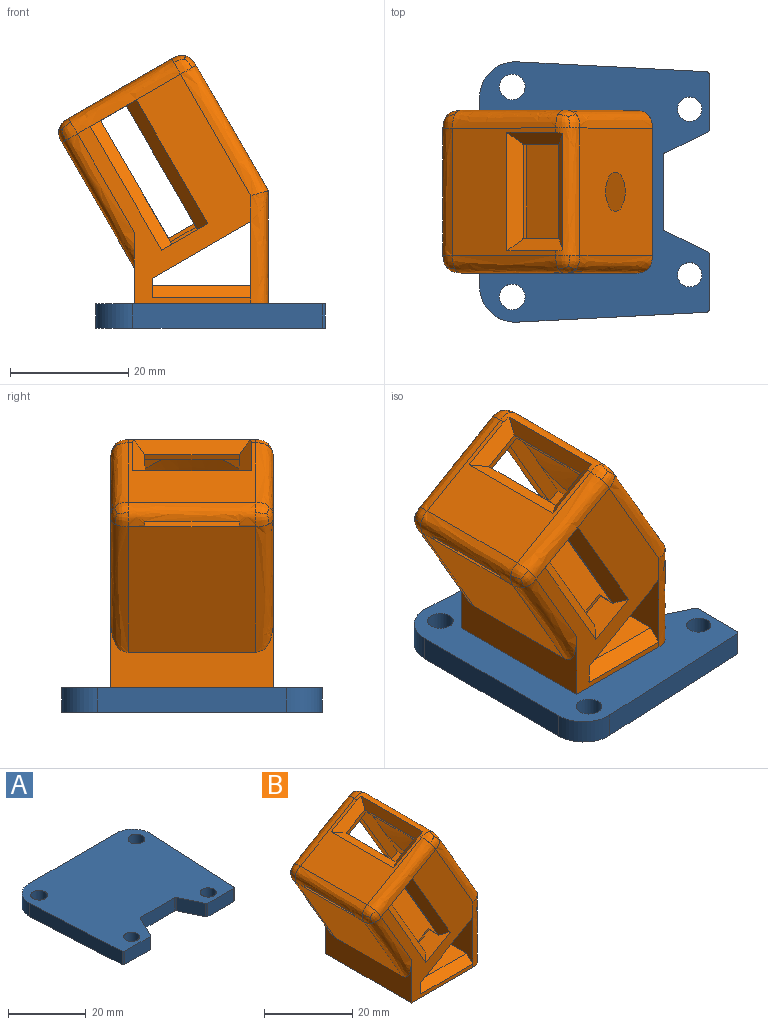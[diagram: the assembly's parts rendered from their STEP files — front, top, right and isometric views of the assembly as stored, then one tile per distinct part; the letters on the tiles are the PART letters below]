
ASSEMBLY  parts=2 mates=1
PART A: 22 faces, bbox 44x38.8x4.2 mm
  f0: cylinder r=0.5mm len=4.2mm, axis (0,0,-1), area 2.4mm2, adj f1,f19,f20,f21
  f1: plane 7.25x4.2mm, normal (0.9,-0.44,0), area 33.8mm2, adj f0,f2,f20,f21
  f2: cylinder r=0.5mm len=4.2mm, axis (0,0,-1), area 2.4mm2, adj f1,f3,f20,f21
  f3: plane 12.28x4.2mm, normal (0,-1,0), area 51.6mm2, adj f2,f4,f20,f21
  f4: cylinder r=0.5mm len=4.2mm, axis (0,0,-1), area 2.4mm2, adj f3,f5,f20,f21
  f5: plane 7.25x4.2mm, normal (-0.9,-0.44,0), area 33.8mm2, adj f4,f6,f20,f21
  f6: cylinder r=0.5mm len=4.2mm, axis (0,0,-1), area 2.4mm2, adj f5,f7,f20,f21
  f7: plane 9.29x4.2mm, normal (0,-1,0), area 39mm2, adj f6,f8,f20,f21
  f8: cylinder r=0.5mm len=4.2mm, axis (0,0,-1), area 3.2mm2, adj f7,f9,f20,f21
  f9: plane 32.04x4.2mm, normal (1,-0.05,0), area 134.7mm2, adj f8,f10,f20,f21
  f10: cylinder r=6mm len=6.31mm, axis (0,0,-1), area 40.9mm2, adj f9,f11,f20,f21
  f11: plane 32.02x4.2mm, normal (0,1,0), area 134.5mm2, adj f10,f12,f20,f21
  f12: cylinder r=6mm len=6.31mm, axis (0,0,-1), area 40.9mm2, adj f11,f13,f20,f21
  f13: plane 32.04x4.2mm, normal (-1,-0.05,0), area 134.7mm2, adj f12,f14,f20,f21
  f14: cylinder r=0.5mm len=4.2mm, axis (0,0,-1), area 3.2mm2, adj f13,f19,f20,f21
  f15: cylinder r=2.17mm len=4.35mm, axis (0,0,-1), area 57.3mm2, adj f20,f21
  f16: cylinder r=2.06mm len=4.2mm, axis (0,0,-1), area 54.4mm2, adj f20,f21
  f17: cylinder r=2.06mm len=4.2mm, axis (0,0,-1), area 54.4mm2, adj f20,f21
  f18: cylinder r=2.17mm len=4.35mm, axis (0,0,-1), area 57.3mm2, adj f20,f21
  f19: plane 9.29x4.2mm, normal (0,-1,0), area 39mm2, adj f0,f14,f20,f21
  f20: plane 44.02x38.82mm, normal (0,0,1), area 1451.3mm2, adj f0,f1,f2,f3,f4,f5,f6,f7
  f21: plane 44.02x38.82mm, normal (0,0,-1), area 1451.3mm2, adj f0,f1,f2,f3,f4,f5,f6,f7
PART B: 66 faces, bbox 37x30.9x44.5 mm
  f0: plane 8.91x7.39mm, normal (-0.87,0,-0.5), area 23.8mm2, adj f3,f22,f65
  f1: plane 8.91x7.39mm, normal (-0.87,0,-0.5), area 23.8mm2, adj f22,f23,f65
  f2: plane 11.58x7.65mm, normal (-0.87,0,-0.5), area 26.7mm2, adj f19,f23,f65
  f3: plane 26.58x22.34mm, normal (0,1,0), area 287.4mm2, adj f0,f19,f20,f22,f26,f65
  f4: plane 21.5x17.45mm, normal (-0.5,0,0.87), area 242.7mm2, adj f33,f34,f36,f48,f55,f56,f60
  f5: plane 27.5x16.64mm, normal (0.5,0,-0.87), area 528.4mm2, adj f6,f13,f14,f15
  f6: plane 27.5x12.88mm, normal (-1,0,0), area 303.1mm2, adj f5,f7,f29,f30,f50,f53
  f7: plane 23.5x16.64mm, normal (0,0,1), area 391.1mm2, adj f6,f13,f29,f30
  f8: plane 21.5x21.22mm, normal (-0.87,0,-0.5), area 526.7mm2, adj f9,f37,f47,f48,f49
  f9: plane 27.5x12mm, normal (-1,0,0), area 171mm2, adj f8,f10,f14,f15,f47,f49
  f10: plane 27.5x22.64mm, normal (0,0,-1), area 619.6mm2, adj f9,f11,f14,f15,f50,f53
  f11: plane 21.5x19.07mm, normal (1,0,0), area 410.1mm2, adj f10,f12,f50,f53
  f12: plane 21.5x21.22mm, normal (0.87,0,0.5), area 492.1mm2, adj f11,f54,f57,f60,f65
  f13: plane 27.5x3.27mm, normal (1,0,0), area 38.9mm2, adj f5,f7,f14,f15,f29,f30
  f14: plane 38.79x29.29mm, normal (0,-1,0), area 378.2mm2, adj f5,f9,f10,f13,f28,f30,f31,f32
  f15: plane 38.79x29.29mm, normal (0,1,0), area 159mm2, adj f5,f9,f10,f13,f29,f49,f53,f56
  f16: plane 20.05x12.22mm, normal (0,-1,0), area 22.6mm2, adj f18,f19,f36,f37,f38,f48
  f17: plane 20.05x12.22mm, normal (0,1,0), area 22.6mm2, adj f18,f19,f33,f37,f38,f48
  f18: plane 16x0.87mm, normal (-0.87,0,-0.5), area 16mm2, adj f16,f17,f19,f35
  f19: plane 25.33x19.49mm, normal (0.5,0,-0.87), area 207.6mm2, adj f2,f3,f16,f17,f18,f20,f21,f23
  f20: plane 11.58x7.65mm, normal (-0.87,0,-0.5), area 26.7mm2, adj f3,f19,f65
  f21: plane 23.15x20.53mm, normal (0.87,0,0.5), area 548.7mm2, adj f19,f22,f23,f24,f37
  f22: plane 23.76x20.14mm, normal (-0.5,0,0.87), area 506.9mm2, adj f0,f1,f3,f21,f23,f24,f25,f26
  f23: plane 31.78x31.34mm, normal (0,-1,0), area 96.6mm2, adj f1,f2,f19,f21,f22,f61,f62,f63
  f24: plane 23.22x16.51mm, normal (0,1,0), area 127.6mm2, adj f19,f21,f22,f27
  f25: plane 4.58x2.93mm, normal (0,-1,0), area 2.5mm2, adj f22,f26,f27,f28
  f26: plane 20.96x12.1mm, normal (-0.87,0,-0.5), area 5.6mm2, adj f3,f19,f22,f25,f28,f31
  f27: plane 20.96x12.1mm, normal (0.87,0,0.5), area 5.6mm2, adj f19,f22,f24,f25,f28,f32
  f28: plane 7.79x5mm, normal (-0.5,0,0.87), area 29mm2, adj f14,f25,f26,f27,f31,f32
  f29: plane 16.64x2mm, normal (0,0.71,0.71), area 47.1mm2, adj f6,f7,f13,f15
  f30: plane 16.64x2mm, normal (0,-0.71,0.71), area 47.1mm2, adj f6,f7,f13,f14
  f31: plane 21.96x13.83mm, normal (-0.61,-0.71,-0.35), area 68.4mm2, adj f14,f19,f26,f28
  f32: plane 21.96x13.83mm, normal (0.61,-0.71,0.35), area 68.4mm2, adj f14,f19,f27,f28
  f33: plane 9.55x6.07mm, normal (-0.35,0.71,0.61), area 25.3mm2, adj f4,f17,f34,f35,f60
  f34: plane 20x2.73mm, normal (0.26,0,0.97), area 50.9mm2, adj f4,f33,f36,f38
  f35: plane 19.64x2.48mm, normal (-0.97,0,0.26), area 45.8mm2, adj f18,f33,f36,f60
  f36: plane 9.55x6.07mm, normal (-0.35,-0.71,0.61), area 25.3mm2, adj f4,f16,f34,f35,f60
  f37: plane 16x1.83mm, normal (-0.5,0,0.87), area 33.8mm2, adj f8,f16,f17,f21
  f38: plane 16x13.44mm, normal (0.5,0,-0.87), area 248.4mm2, adj f16,f17,f34,f48
  f39: bspline ~3.07x2.56mm, area 5.2mm2, adj f40,f56,f57,f59
  f40: bspline ~2.32x2.25mm, area 5.2mm2, adj f39,f56,f59,f60
  f41: bspline ~3.07x2.56mm, area 5.2mm2, adj f42,f54,f55,f58
  f42: bspline ~2.25x1.95mm, area 5.2mm2, adj f41,f54,f58,f60
  f43: bspline ~2.32x2.25mm, area 5.2mm2, adj f44,f48,f49,f52
  f44: bspline ~2.25x1.95mm, area 5.2mm2, adj f43,f48,f52,f56
  f45: bspline ~2.32x2.25mm, area 5.2mm2, adj f46,f47,f48,f51
  f46: bspline ~3.07x2.56mm, area 5.2mm2, adj f45,f47,f51,f55
  f47: bspline ~22.72x14.85mm, area 110.7mm2, adj f8,f9,f14,f45,f46
  f48: bspline ~30.25x4.1mm, area 88.6mm2, adj f4,f8,f16,f17,f38,f43,f44,f45
  f49: bspline ~22.72x14.85mm, area 110.7mm2, adj f8,f9,f15,f43,f52
  f50: bspline ~20.98x3mm, area 90.9mm2, adj f6,f10,f11,f14,f54
  f51: bspline ~2.25x1.95mm, area 5.2mm2, adj f45,f46,f48,f55
  f52: bspline ~3.07x2.56mm, area 5.2mm2, adj f43,f44,f49,f56
  f53: bspline ~20.98x3mm, area 90.9mm2, adj f6,f10,f11,f15,f57
  f54: bspline ~22.72x14.85mm, area 117.3mm2, adj f12,f14,f41,f42,f50
  f55: bspline ~18.95x12.67mm, area 98.1mm2, adj f4,f14,f19,f41,f46,f51,f58
  f56: bspline ~18.95x12.67mm, area 98.1mm2, adj f4,f15,f39,f40,f44,f52
  f57: bspline ~22.72x14.85mm, area 117.3mm2, adj f12,f15,f39,f53,f59
  f58: bspline ~2.32x2.25mm, area 5.2mm2, adj f41,f42,f55,f60
  f59: bspline ~2.25x1.95mm, area 5.2mm2, adj f39,f40,f57,f60
  f60: bspline ~30.25x4.1mm, area 78.6mm2, adj f4,f12,f33,f35,f36,f40,f42,f58
  f61: plane 19.87x11.58mm, normal (0.86,0,0.5), area 50mm2, adj f15,f23,f62,f64
  f62: plane 16.42x9.57mm, normal (0.5,0,-0.86), area 41.3mm2, adj f15,f23,f61,f63
  f63: plane 19.87x11.58mm, normal (-0.86,0,-0.5), area 50mm2, adj f15,f23,f62,f64
  f64: plane 16.42x9.57mm, normal (-0.5,0,0.86), area 41.3mm2, adj f15,f23,f61,f63
  f65: cone r=12mm half-angle=80deg, axis (-0.87,0,-0.5), area 420.5mm2, adj f0,f1,f2,f3,f12,f20,f22,f23
PLACE A rot(axis=(0,0,1),90deg) t=(-18.15,-13.32,-19.35)mm
PLACE B t=(-20.38,-13.32,4.65)mm
MATE fastened A.f20 <-> B.f10  axis (0,0,1) through (-23.56,-13.32,-15.15)mm
